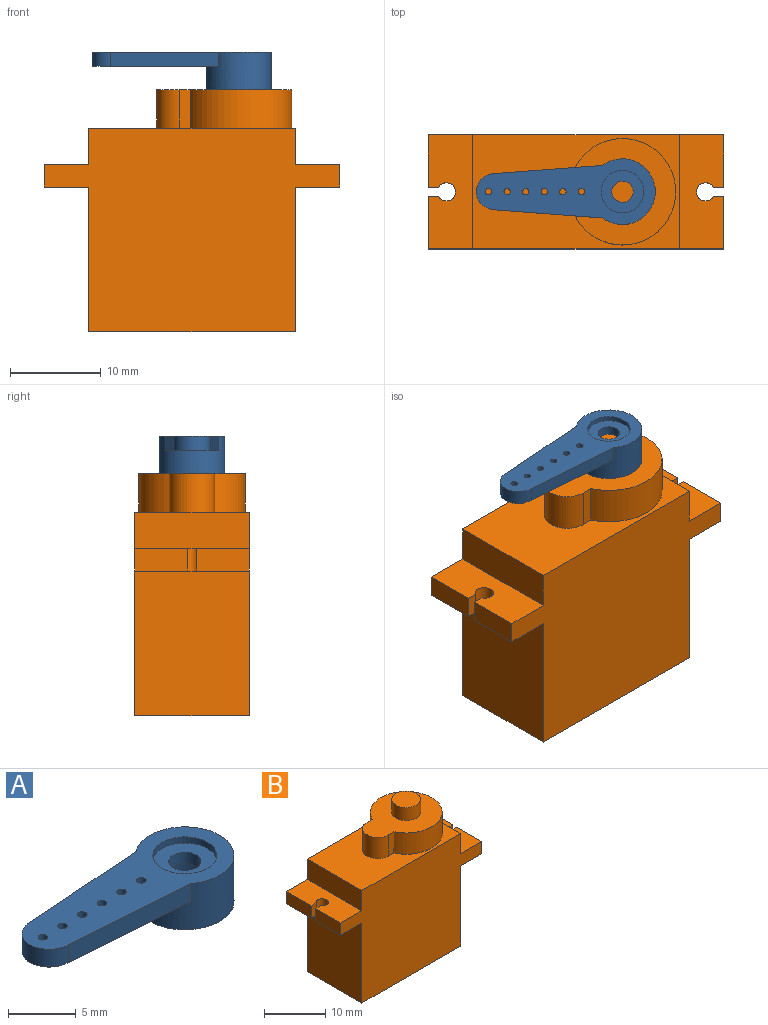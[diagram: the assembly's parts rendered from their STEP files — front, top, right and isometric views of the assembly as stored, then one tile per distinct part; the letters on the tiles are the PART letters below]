
ASSEMBLY  parts=2 mates=1
PART A: 18 faces, bbox 19.8x7.3x4.2 mm
  f0: cylinder r=2.35mm len=4.7mm, axis (0,0,-1), area 38.4mm2, adj f13,f15
  f1: cylinder r=3.62mm len=7.25mm, axis (0,0,-1), area 83.8mm2, adj f2,f9,f12,f13,f17
  f2: plane 11.95x1.6mm, normal (-0.08,1,0), area 19.2mm2, adj f1,f3,f12,f17
  f3: cylinder r=2mm len=4mm, axis (0,0,-1), area 10.1mm2, adj f2,f9,f12,f17
  f4: cylinder r=0.35mm len=1.6mm, axis (0,0,-1), area 3.5mm2, adj f12,f17
  f5: cylinder r=0.35mm len=1.6mm, axis (0,0,-1), area 3.5mm2, adj f12,f17
  f6: cylinder r=0.35mm len=1.6mm, axis (0,0,-1), area 3.5mm2, adj f12,f17
  f7: cylinder r=0.35mm len=1.6mm, axis (0,0,-1), area 3.5mm2, adj f12,f17
  f8: cylinder r=0.35mm len=1.6mm, axis (0,0,-1), area 3.5mm2, adj f12,f17
  f9: plane 11.95x1.6mm, normal (-0.08,-1,0), area 19.2mm2, adj f1,f3,f12,f17
  f10: cylinder r=2.35mm len=4.7mm, axis (0,0,-1), area 8.1mm2, adj f12,f14
  f11: cylinder r=0.35mm len=1.6mm, axis (0,0,-1), area 3.5mm2, adj f12,f17
  f12: plane 19.75x7.25mm, normal (0,0,1), area 80.6mm2, adj f1,f2,f3,f4,f5,f6,f7,f8
  f13: plane 7.25x7.25mm, normal (0,0,-1), area 23.9mm2, adj f0,f1
  f14: plane 4.7x4.7mm, normal (0,0,1), area 13mm2, adj f10,f16
  f15: plane 4.7x4.7mm, normal (0,0,-1), area 13mm2, adj f0,f16
  f16: cylinder r=1.18mm len=2.35mm, axis (0,0,-1), area 7.4mm2, adj f14,f15
  f17: plane 13.95x5.8mm, normal (0,0,-1), area 56.7mm2, adj f1,f2,f3,f4,f5,f6,f7,f8
PART B: 29 faces, bbox 32.6x12.6x29.4 mm
  f0: plane 22.8x12.6mm, normal (0,0,1), area 164.9mm2, adj f3,f4,f5,f6,f22,f23,f24,f25
  f1: plane 16x12.6mm, normal (-1,0,0), area 201.6mm2, adj f4,f6,f7,f21
  f2: plane 16x12.6mm, normal (1,0,0), area 201.6mm2, adj f4,f6,f7,f14
  f3: plane 12.6x4.05mm, normal (1,0,0), area 51mm2, adj f0,f4,f6,f13
  f4: plane 32.6x22.5mm, normal (0,1,0), area 537mm2, adj f0,f1,f2,f3,f5,f7,f12,f13
  f5: plane 12.6x4.05mm, normal (-1,0,0), area 51mm2, adj f0,f4,f6,f20
  f6: plane 32.6x22.5mm, normal (0,-1,0), area 537mm2, adj f0,f1,f2,f3,f5,f7,f8,f13
  f7: plane 22.8x12.6mm, normal (0,0,-1), area 287.3mm2, adj f1,f2,f4,f6
  f8: plane 5.8x2.45mm, normal (1,0,0), area 14.2mm2, adj f6,f9,f13,f14
  f9: plane 2.45x1.13mm, normal (0,1,0), area 2.8mm2, adj f8,f10,f13,f14
  f10: cylinder r=1mm len=2.45mm, axis (0,0,-1), area 12.8mm2, adj f9,f11,f13,f14
  f11: plane 2.45x1.13mm, normal (0,-1,0), area 2.8mm2, adj f10,f12,f13,f14
  f12: plane 5.8x2.45mm, normal (1,0,0), area 14.2mm2, adj f4,f11,f13,f14
  f13: plane 12.6x4.9mm, normal (0,0,1), area 57.6mm2, adj f3,f4,f6,f8,f9,f10,f11,f12
  f14: plane 12.6x4.9mm, normal (0,0,-1), area 57.6mm2, adj f2,f4,f6,f8,f9,f10,f11,f12
  f15: plane 5.8x2.45mm, normal (-1,0,0), area 14.2mm2, adj f4,f16,f20,f21
  f16: plane 2.45x1.13mm, normal (0,-1,0), area 2.8mm2, adj f15,f17,f20,f21
  f17: cylinder r=1mm len=2.45mm, axis (0,0,-1), area 12.8mm2, adj f16,f18,f20,f21
  f18: plane 2.45x1.13mm, normal (0,1,0), area 2.8mm2, adj f17,f19,f20,f21
  f19: plane 5.8x2.45mm, normal (-1,0,0), area 14.2mm2, adj f6,f18,f20,f21
  f20: plane 12.6x4.9mm, normal (0,0,1), area 57.6mm2, adj f4,f5,f6,f15,f16,f17,f18,f19
  f21: plane 12.6x4.9mm, normal (0,0,-1), area 57.6mm2, adj f1,f4,f6,f15,f16,f17,f18,f19
  f22: plane 4.25x1.21mm, normal (0,1,0), area 5.1mm2, adj f0,f23,f25,f26
  f23: cylinder r=2.5mm len=5mm, axis (0,0,-1), area 33.4mm2, adj f0,f22,f24,f26
  f24: plane 4.25x1.21mm, normal (0,-1,0), area 5.1mm2, adj f0,f23,f25,f26
  f25: cylinder r=5.88mm len=11.75mm, axis (0,0,-1), area 134.9mm2, adj f0,f22,f24,f26
  f26: plane 14.9x11.75mm, normal (0,0,1), area 105.1mm2, adj f22,f23,f24,f25,f27
  f27: cylinder r=2.35mm len=4.7mm, axis (0,0,-1), area 38.4mm2, adj f26,f28
  f28: plane 4.7x4.7mm, normal (0,0,1), area 17.3mm2, adj f27
PLACE A rot(axis=(0,0,1),0deg) t=(-7.94,-1.76,-1.14)mm
PLACE B t=(-7.94,-1.76,-1.14)mm fixed
MATE revolute A.f0 <-> B.f27  axis (0,0,-1) through (-2.81,-1.76,25.61)mm
